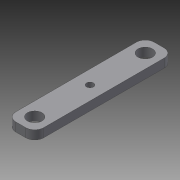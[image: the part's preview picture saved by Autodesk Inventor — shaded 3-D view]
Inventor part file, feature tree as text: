
AUTODESK INVENTOR PART (.ipt)
format: ipt  version: 2015 (Build 190159000, 159)  size: 98,304 bytes
history: native  units: in
note: dims shown in document units (in); Inventor stores cm internally (conversion verified against a paired STEP export)
features: extrude x1, sketch x1
ambient origin geometry x8: Origin, YZ Plane, XZ Plane, XY Plane, X Axis, Y Axis, Z Axis, Center Point
bodies: Solid1 (feature_tree)
feature tree (2):
  extrude  "Extrusion1"  Depth=0.7874in
  sketch  "Sketch1"  dims[d0=3.937in d1=0.7874in d2=0.4134in d3=3.1496in d4=0.25in d5=0.25in d6=0.0in d7=0.2in]
